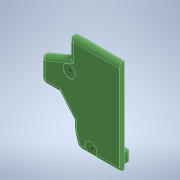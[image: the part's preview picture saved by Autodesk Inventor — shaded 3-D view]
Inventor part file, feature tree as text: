
AUTODESK INVENTOR PART (.ipt)
format: ipt  version: 2022 (Build 260153000, 153)  size: 477,184 bytes
history: native  units: mm
features: extrude x4, fillet x3, other x1, sketch x1, chamfer x1
ambient origin geometry x8: Origin, YZ Plane, XZ Plane, XY Plane, X Axis, Y Axis, Z Axis, Center Point
bodies: Body1 (feature_tree)
feature tree (10):
  other  "Твердое тело1"
  sketch  "Эскиз1"
  extrude  "Выдавливание1"  Depth=20.0mm
  extrude  "Выдавливание3"  Depth=50.0mm
  chamfer  "Фаска1"  Distance=40.0mm
  fillet  "Сопряжение1"  Radius=2.5mm
  extrude  "Выдавливание4"  Depth=7.0mm TaperAngle=0.0deg
  extrude  "Выдавливание5"  Depth=2.5mm TaperAngle=45.0deg
  fillet  "Сопряжение3"  Radius=2.0mm
  fillet  "Сопряжение4"  Radius=37.7mm
